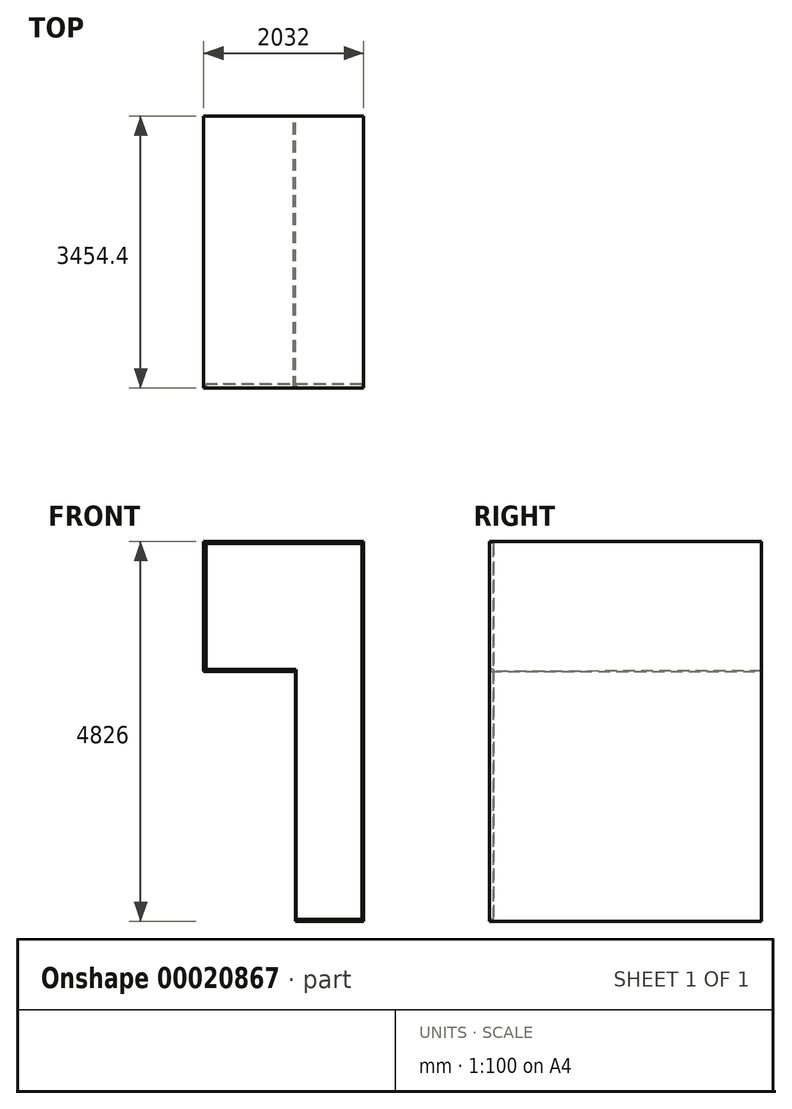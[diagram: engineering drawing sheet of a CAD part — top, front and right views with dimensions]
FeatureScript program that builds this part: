
annotation { "Feature Type Name" : "Feature", "Feature Type Description" : "" }
export const myFeature = defineFeature(function(context is Context, id is Id, definition is map)
    precondition{}
    {
        {
            var Q0;
            Q0=qCreatedBy(makeId("Front.planeOp"),FACE);
            var sketch = newSketch(context, id + "F0", { "sketchPlane" : qUnion([Q0])});
            skLineSegment(sketch, "E0", {"start": v(-60.38, 1641.44) * mm, "end": v(1971.62, 1641.44) * mm});
            skLineSegment(sketch, "E1", {"start": v(1971.62, 1641.44) * mm, "end": v(1971.62, -9.56) * mm});
            skLineSegment(sketch, "E2", {"start": v(1082.62, -9.56) * mm, "end": v(-60.38, -9.56) * mm});
            skLineSegment(sketch, "E3", {"start": v(-60.38, -9.56) * mm, "end": v(-60.38, 1641.44) * mm});
            skLineSegment(sketch, "E4", {"start": v(1971.62, -9.56) * mm, "end": v(1971.62, -3184.56) * mm});
            skLineSegment(sketch, "E5", {"start": v(1971.62, -3184.56) * mm, "end": v(1082.62, -3184.56) * mm});
            skLineSegment(sketch, "E6", {"start": v(1082.62, -3184.56) * mm, "end": v(1082.62, -9.56) * mm});
            skSolve(sketch);
        }
        {
            var Q0;
            Q0=makeQuery(id+"F0.imprint","IMPRINT",FACE,{"disambiguationData":[TD([[makeQuery(id+"F0.imprint","IMPRINT",EDGE,{"derivedFrom":sQuery(id+"F0.wireOp",EDGE,"E0")}),-1.0]])]});
            extrude(context, id + "F1", {"entities" : qUnion([Q0]), "depth" : 3454.4 * mm});
        }
        {
            var Q0;
            Q0=makeQuery(id+"F1.opExtrude","CAP_FACE",FACE,{"disambiguationData":[OSD([sQuery(id+"F0.wireOp",EDGE,"E0"),sQuery(id+"F0.wireOp",EDGE,"E1"),sQuery(id+"F0.wireOp",EDGE,"E2"),sQuery(id+"F0.wireOp",EDGE,"E3"),sQuery(id+"F0.wireOp",EDGE,"E4"),sQuery(id+"F0.wireOp",EDGE,"E5"),sQuery(id+"F0.wireOp",EDGE,"E6")])],"isStart":false});
            var sketch = newSketch(context, id + "F2", { "sketchPlane" : qUnion([Q0])});
            skLineSegment(sketch, "E7", {"start": v(-34.8, 1617.44) * mm, "end": v(-34.8, 18.69) * mm});
            skLineSegment(sketch, "E8", {"start": v(-34.8, 18.69) * mm, "end": v(1109.15, 18.69) * mm});
            skLineSegment(sketch, "E9", {"start": v(1109.15, 18.69) * mm, "end": v(1109.15, -3158.27) * mm});
            skLineSegment(sketch, "E10", {"start": v(1109.15, -3158.27) * mm, "end": v(1946.81, -3158.27) * mm});
            skLineSegment(sketch, "E11", {"start": v(1946.81, -3158.27) * mm, "end": v(1946.81, 1616.8) * mm});
            skLineSegment(sketch, "E12", {"start": v(1946.81, 1616.8) * mm, "end": v(-34.8, 1617.44) * mm});
            skSolve(sketch);
        }
        {
            var Q0;
            Q0=makeQuery(id+"F2.imprint","IMPRINT",FACE,{"disambiguationData":[TD([[makeQuery(id+"F2.imprint","IMPRINT",EDGE,{"derivedFrom":sQuery(id+"F2.wireOp",EDGE,"E7")}),1.0]])]});
            var Q1;
            Q1 = qConstructionFilter(qBodyType(qCreatedBy(id + "F2" ,EDGE), BodyType.WIRE), ConstructionObject.NO);
            extrude(context, id + "F3", {"entities" : qUnion([Q0]), "operationType" : NewBodyOperationType.REMOVE, "surfaceEntities" : qUnion([Q1]), "oppositeDirection" : true, "depth" : 50.8 * mm});
        }
        {
            var Q0;
            Q0=makeQuery(id+"F1.opExtrude","SWEPT_FACE",FACE,{"disambiguationData":[OSD([sQuery(id+"F0.wireOp",EDGE,"E6")])]});
            var sketch = newSketch(context, id + "F4", { "sketchPlane" : qUnion([Q0])});
            skLineSegment(sketch, "E13", {"start": v(3454.4, -3184.56) * mm, "end": v(0, -3184.56) * mm});
            skLineSegment(sketch, "E14", {"start": v(0, -3184.56) * mm, "end": v(0, 0) * mm});
            skLineSegment(sketch, "E15", {"start": v(0, 0) * mm, "end": v(3454.4, -9.56) * mm});
            skLineSegment(sketch, "E16", {"start": v(3454.4, -9.56) * mm, "end": v(3454.4, -3184.56) * mm});
            skSolve(sketch);
        }
        {
            var Q0;
            Q0 = qSketchRegion(id + "F4", true);
            extrude(context, id + "F5", {"entities" : qUnion([Q0]), "operationType" : NewBodyOperationType.REMOVE, "oppositeDirection" : true, "depth" : 25.4 * mm});
        }
    });
